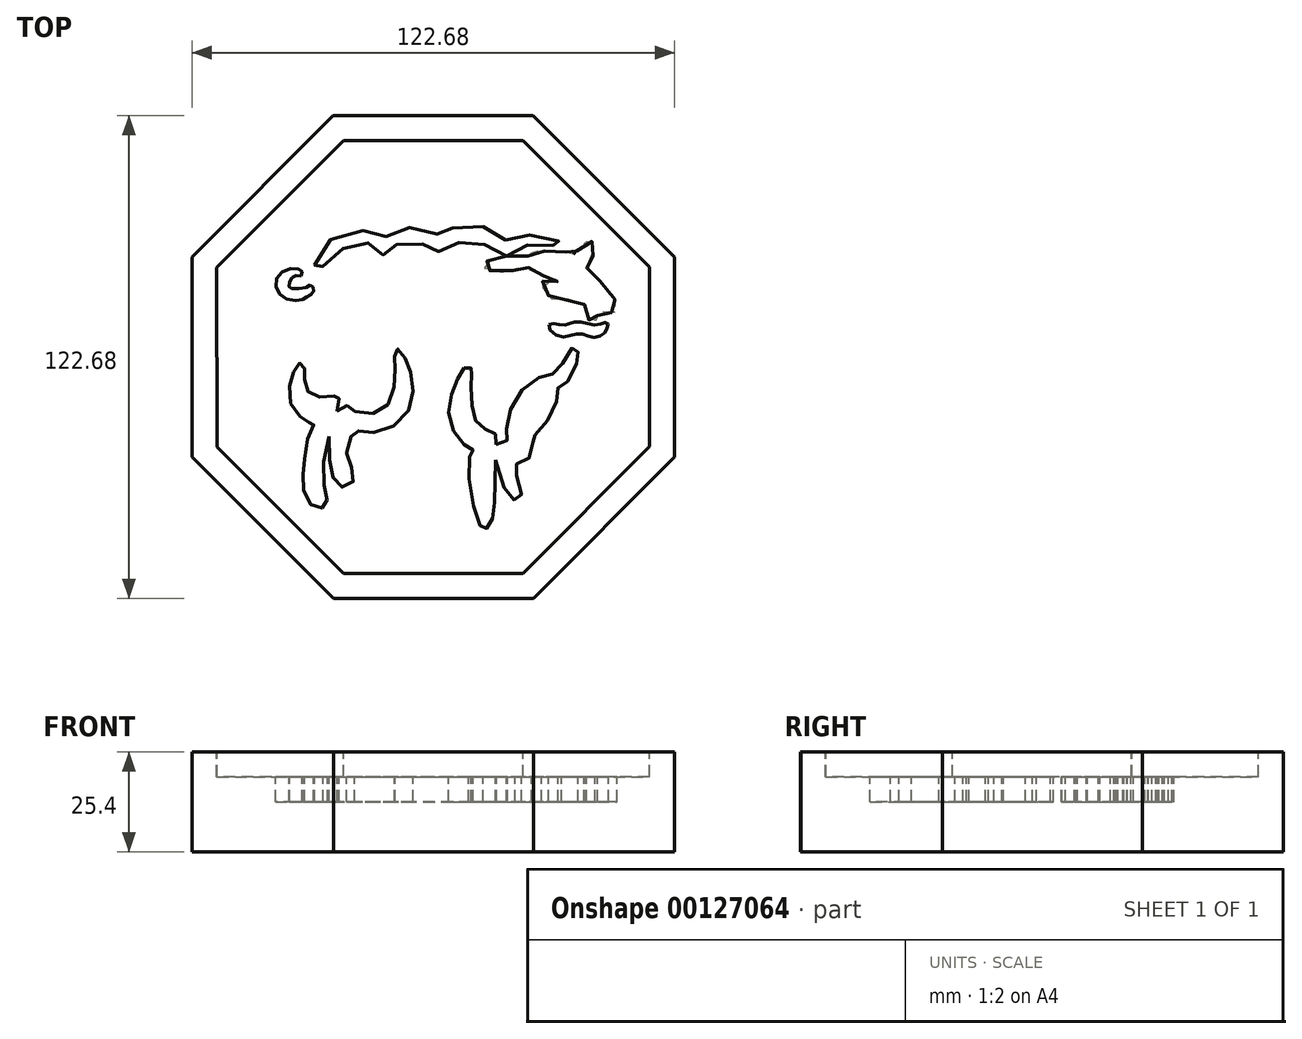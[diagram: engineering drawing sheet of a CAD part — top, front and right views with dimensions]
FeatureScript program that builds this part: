
annotation { "Feature Type Name" : "Feature", "Feature Type Description" : "" }
export const myFeature = defineFeature(function(context is Context, id is Id, definition is map)
    precondition{}
    {
        {
            var Q0;
            Q0=qCreatedBy(makeId("Top.planeOp"),FACE);
            var sketch = newSketch(context, id + "F0", { "sketchPlane" : qUnion([Q0])});
            skCircle(sketch, "E0.cCircle", {"center": v(0, 0) * mm, "radius": 61.32 * mm, "construction": true});
            skLineSegment(sketch, "E0.0", {"start": v(-61.3, -25.44) * mm, "end": v(-61.34, 25.36) * mm});
            skLineSegment(sketch, "E0.1", {"start": v(-61.34, 25.36) * mm, "end": v(-25.44, 61.3) * mm});
            skLineSegment(sketch, "E0.2", {"start": v(-25.44, 61.3) * mm, "end": v(25.36, 61.34) * mm});
            skLineSegment(sketch, "E0.3", {"start": v(25.36, 61.34) * mm, "end": v(61.3, 25.44) * mm});
            skLineSegment(sketch, "E0.4", {"start": v(61.3, 25.44) * mm, "end": v(61.34, -25.36) * mm});
            skLineSegment(sketch, "E0.5", {"start": v(61.34, -25.36) * mm, "end": v(25.44, -61.3) * mm});
            skLineSegment(sketch, "E0.6", {"start": v(25.44, -61.3) * mm, "end": v(-25.36, -61.34) * mm});
            skLineSegment(sketch, "E0.7", {"start": v(-25.36, -61.34) * mm, "end": v(-61.3, -25.44) * mm});
            skPoint(sketch, "E0.0.midPoint", {"position": v(-61.32, -0.04) * mm});
            skSolve(sketch);
        }
        {
            var Q0;
            Q0=qSketchRegion(id+"F0",true);
            extrude(context, id + "F1", {"entities" : qUnion([Q0]), "depth" : 25.4 * mm});
        }
        {
            var Q0;
            Q0=makeQuery(id+"F1.opExtrude","CAP_FACE",FACE,{"disambiguationData":[OSD([sQuery(id+"F0.wireOp",EDGE,"E0.0"),sQuery(id+"F0.wireOp",EDGE,"E0.1"),sQuery(id+"F0.wireOp",EDGE,"E0.2"),sQuery(id+"F0.wireOp",EDGE,"E0.3"),sQuery(id+"F0.wireOp",EDGE,"E0.4"),sQuery(id+"F0.wireOp",EDGE,"E0.5"),sQuery(id+"F0.wireOp",EDGE,"E0.6"),sQuery(id+"F0.wireOp",EDGE,"E0.7")])],"isStart":false});
            var sketch = newSketch(context, id + "F2", { "sketchPlane" : qUnion([Q0])});
            skLineSegment(sketch, "E1.0", {"start": v(-54.96, -22.8) * mm, "end": v(-54.99, 22.73) * mm});
            skLineSegment(sketch, "E1.1", {"start": v(-22.73, -54.99) * mm, "end": v(-54.96, -22.8) * mm});
            skLineSegment(sketch, "E1.2", {"start": v(-54.99, 22.73) * mm, "end": v(-22.8, 54.96) * mm});
            skLineSegment(sketch, "E1.3", {"start": v(22.8, -54.96) * mm, "end": v(-22.73, -54.99) * mm});
            skLineSegment(sketch, "E1.4", {"start": v(-22.8, 54.96) * mm, "end": v(22.73, 54.99) * mm});
            skLineSegment(sketch, "E1.5", {"start": v(22.73, 54.99) * mm, "end": v(54.96, 22.8) * mm});
            skLineSegment(sketch, "E1.6", {"start": v(54.96, 22.8) * mm, "end": v(54.99, -22.73) * mm});
            skLineSegment(sketch, "E1.7", {"start": v(54.99, -22.73) * mm, "end": v(22.8, -54.96) * mm});
            skSolve(sketch);
        }
        {
            var Q0;
            Q0=qSketchRegion(id+"F2",true);
            extrude(context, id + "F3", {"entities" : qUnion([Q0]), "operationType" : NewBodyOperationType.REMOVE, "oppositeDirection" : true, "depth" : 6.35 * mm});
        }
        {
            var Q0;
            Q0=makeQuery(id+"F3.boolean.opBoolean","COPY",FACE,{"derivedFrom":makeQuery(id+"F3.opExtrude","CAP_FACE",FACE,{"disambiguationData":[OSD([sQuery(id+"F2.wireOp",EDGE,"E1.0"),sQuery(id+"F2.wireOp",EDGE,"E1.1"),sQuery(id+"F2.wireOp",EDGE,"E1.2"),sQuery(id+"F2.wireOp",EDGE,"E1.3"),sQuery(id+"F2.wireOp",EDGE,"E1.4"),sQuery(id+"F2.wireOp",EDGE,"E1.5"),sQuery(id+"F2.wireOp",EDGE,"E1.6"),sQuery(id+"F2.wireOp",EDGE,"E1.7")])],"isStart":false})});
            var sketch = newSketch(context, id + "F4", { "sketchPlane" : qUnion([Q0])});
            skFitSpline(sketch, "E2", {"points": [v(-33.6, 20.58) * mm, v(-34.85, 20.67) * mm, v(-35.77, 20.24) * mm, v(-36.5, 19.3) * mm, v(-36.57, 17.98) * mm, v(-36.57, 17.58) * mm, v(-34.76, 17.43) * mm, v(-32.34, 17.64) * mm, v(-31.33, 18.28) * mm, v(-30.75, 18) * mm, v(-30.44, 17.36) * mm, v(-30.47, 16.48) * mm, v(-31.18, 15.83) * mm, v(-32.52, 15) * mm, v(-33.38, 14.55) * mm, v(-36.63, 14.48) * mm, v(-39.56, 16.83) * mm, v(-39.83, 20.04) * mm, v(-36.78, 22.35) * mm, v(-33.85, 22.27) * mm, v(-33.37, 21.57) * mm, v(-33.6, 20.58) * mm]});
            skFitSpline(sketch, "E3", {"points": [v(29.34, 8.27) * mm, v(30.02, 6.42) * mm, v(32.99, 5.06) * mm, v(35.32, 5.64) * mm, v(37.36, 5.93) * mm, v(39.26, 5.4) * mm, v(41.2, 4.96) * mm, v(42.9, 5.7) * mm, v(43.93, 6.71) * mm, v(44.41, 8.02) * mm, v(44.32, 8.7) * mm, v(43.2, 8.7) * mm, v(41.84, 8.17) * mm, v(39.36, 8.51) * mm, v(37.12, 8.95) * mm, v(35.08, 8.75) * mm, v(34.1, 8.22) * mm, v(32.35, 8.27) * mm, v(30.65, 8.46) * mm, v(29.34, 8.27) * mm]});
            skFitSpline(sketch, "E4", {"points": [v(27.54, 19.16) * mm, v(27.98, 17.22) * mm, v(29.58, 15.22) * mm, v(30.7, 14.6) * mm, v(34.4, 14.69) * mm, v(38.24, 13.86) * mm, v(38.34, 12.06) * mm, v(39.02, 10.12) * mm, v(39.99, 9.1) * mm, v(41.01, 9.2) * mm, v(41.7, 10.16) * mm, v(41.74, 11.23) * mm, v(43.88, 11.43) * mm, v(46.31, 11.43) * mm, v(46.55, 13.23) * mm, v(45.1, 16.54) * mm, v(41.98, 19.7) * mm, v(40.04, 21.54) * mm, v(38.92, 22.8) * mm, v(39.21, 23.78) * mm, v(40.38, 25.34) * mm, v(41.1, 28.16) * mm, v(40.82, 29.18) * mm, v(39.21, 29.28) * mm, v(36.73, 27.38) * mm, v(35.9, 26.4) * mm, v(35.7, 26.17) * mm, v(34.54, 26.5) * mm, v(32.11, 26.85) * mm, v(28.37, 26.94) * mm, v(24.72, 26.21) * mm, v(24.33, 25.68) * mm, v(21.8, 25.63) * mm, v(17.9, 25.63) * mm, v(15.14, 24.85) * mm, v(12.75, 23.78) * mm, v(12.75, 22.9) * mm, v(14.94, 21.84) * mm, v(19.22, 21.74) * mm, v(21.75, 22.61) * mm, v(23.84, 23.05) * mm, v(24.82, 21.74) * mm, v(26.61, 20.67) * mm, v(29.92, 20.67) * mm, v(31.04, 19.7) * mm, v(31.62, 18.92) * mm, v(29.63, 18.97) * mm, v(27.54, 19.16) * mm]});
            skFitSpline(sketch, "E5", {"points": [v(18.56, 25.7) * mm, v(20.83, 27.42) * mm, v(24.47, 28.53) * mm, v(29.01, 28.79) * mm, v(30.9, 28.14) * mm, v(32.11, 27.88) * mm, v(32.58, 28.53) * mm, v(31.16, 29.9) * mm, v(26.42, 31) * mm, v(19.8, 30.28) * mm, v(18.5, 29.63) * mm, v(17.78, 30.41) * mm, v(13.7, 32.88) * mm, v(7.4, 33.4) * mm, v(3.7, 32.1) * mm, v(1.81, 30.54) * mm, v(1.03, 31.12) * mm, v(-2.8, 32.81) * mm, v(-7.8, 32.55) * mm, v(-11.56, 31.06) * mm, v(-12.27, 30.54) * mm, v(-14.48, 31.38) * mm, v(-20.52, 32.03) * mm, v(-26.36, 29.63) * mm, v(-29.58, 24.85) * mm, v(-30.08, 22.18) * mm, v(-29.27, 21.72) * mm, v(-28.8, 22.14) * mm, v(-26.8, 24.42) * mm, v(-23.29, 27.28) * mm, v(-20.24, 28.7) * mm, v(-16.07, 28.82) * mm, v(-13.67, 26.85) * mm, v(-13.1, 26.08) * mm, v(-12.01, 26) * mm, v(-11.44, 26.85) * mm, v(-9.5, 28.47) * mm, v(-6.34, 28.97) * mm, v(-2.1, 28.63) * mm, v(-0.4, 27.86) * mm, v(1.07, 26.85) * mm, v(1.92, 27.16) * mm, v(5.09, 28.86) * mm, v(8.33, 29.13) * mm, v(12.34, 28.74) * mm, v(15.9, 27.43) * mm, v(18.56, 25.7) * mm]});
            skFitSpline(sketch, "E6", {"points": [v(-32.65, -4.03) * mm, v(-32.85, -2.48) * mm, v(-33.72, -1.5) * mm, v(-34.8, -2.57) * mm, v(-36.25, -5.98) * mm, v(-36.25, -11.91) * mm, v(-33.14, -15.7) * mm, v(-31.3, -16.68) * mm, v(-30.22, -16.87) * mm, v(-31.1, -18.33) * mm, v(-32.75, -25.92) * mm, v(-33.14, -30.59) * mm, v(-32.27, -35.84) * mm, v(-29.35, -38.56) * mm, v(-27.11, -37.4) * mm, v(-27.2, -35.06) * mm, v(-27.8, -25.72) * mm, v(-24.48, -13.95) * mm, v(-24, -10.55) * mm, v(-24, -9.87) * mm, v(-26.33, -10.06) * mm, v(-30.42, -9.77) * mm, v(-32.56, -7.63) * mm, v(-32.65, -4.03) * mm]});
            skFitSpline(sketch, "E7", {"points": [v(-9.8, -1.8) * mm, v(-9.9, -6.37) * mm, v(-11.55, -12.1) * mm, v(-16.31, -14.44) * mm, v(-20.98, -13.27) * mm, v(-21.86, -12.4) * mm, v(-23.41, -12.5) * mm, v(-26.44, -20.15) * mm, v(-25.94, -28.84) * mm, v(-24.48, -32.34) * mm, v(-21.66, -33.02) * mm, v(-20, -30.2) * mm, v(-21.66, -26.4) * mm, v(-21.57, -21.93) * mm, v(-19.82, -18.72) * mm, v(-18.55, -18.91) * mm, v(-12.9, -18.82) * mm, v(-6.49, -13.95) * mm, v(-5.22, -7.05) * mm, v(-6.49, -1.7) * mm, v(-7.85, 0.83) * mm, v(-9.31, 2.1) * mm, v(-9.8, 0.93) * mm, v(-9.8, -1.8) * mm]});
            skFitSpline(sketch, "E8", {"points": [v(15.67, -19.48) * mm, v(12.07, -17.73) * mm, v(9.84, -12.77) * mm, v(9.64, -4.89) * mm, v(9.74, -3.43) * mm, v(9.45, -2.65) * mm, v(8.09, -2.65) * mm, v(5.85, -6.45) * mm, v(3.9, -14.71) * mm, v(7.99, -22.4) * mm, v(10.13, -23.66) * mm, v(9.25, -25.41) * mm, v(11.2, -41.27) * mm, v(13.14, -43.7) * mm, v(14.8, -41.66) * mm, v(15.67, -33.78) * mm, v(15.96, -22.2) * mm, v(15.67, -19.48) * mm]});
            skFitSpline(sketch, "E9", {"points": [v(34.93, 1.92) * mm, v(32.6, -1.97) * mm, v(30.55, -4.2) * mm, v(29.58, -4.3) * mm, v(26.08, -5.67) * mm, v(21.5, -9.65) * mm, v(18.98, -15.5) * mm, v(18.69, -19.38) * mm, v(18.88, -20.94) * mm, v(17.81, -21.72) * mm, v(15.96, -22.2) * mm, v(16.64, -29.7) * mm, v(19.66, -35.92) * mm, v(20.92, -36.3) * mm, v(22.29, -35.72) * mm, v(21.8, -32.8) * mm, v(20.83, -28.04) * mm, v(20.92, -27.26) * mm, v(22.48, -26.97) * mm, v(25, -24.63) * mm, v(25.3, -21.42) * mm, v(24.91, -20.94) * mm, v(25.7, -19.97) * mm, v(28.7, -16.56) * mm, v(31.33, -11.3) * mm, v(31.72, -8.4) * mm, v(31.72, -7.61) * mm, v(32.99, -7.03) * mm, v(36, -3.24) * mm, v(36.58, 0) * mm, v(36.78, 1.14) * mm, v(36.1, 2.8) * mm, v(34.93, 1.92) * mm]});
            skSolve(sketch);
        }
        {
            var Q0;
            Q0 = qSketchRegion(id + "F4", true);
            extrude(context, id + "F5", {"entities" : qUnion([Q0]), "operationType" : NewBodyOperationType.REMOVE, "oppositeDirection" : true, "depth" : 6.35 * mm});
        }
    });
